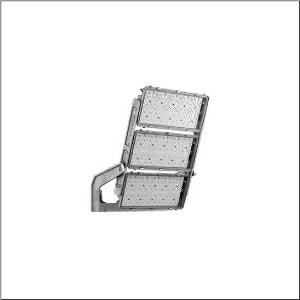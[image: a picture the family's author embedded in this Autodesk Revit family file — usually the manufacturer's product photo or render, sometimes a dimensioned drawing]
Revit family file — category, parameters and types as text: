
# Revit family: floodlight_fl_11_maxi_pro_remote___pl64_5xa779524e01aa_eec4
name_source: partatom
category: Lighting Fixtures
units: mm (PartAtom-declared; Revit-internal decimal feet)

## family parameters
Cut with Voids When Loaded = No
Host = Face
Light Source = No
Part Type = Normal
Room Calculation Point = No
Round Connector Dimension = Use Diameter
Shared = No

## types (1)
- --- (1 x LED, 128450 lm, 1334.7 W, 5700K)
    Apparent Load = 1335 VA
    CIE Flux Codes = 28 80 98 100 100
    Color Rendering = 90
    Color Temperature = 5700K
    Default Elevation = 1800 mm
    Description = Floodlight FL 11  maxi  pro Remote floodlight; light control with lens of PMMA; cover panel of toughened safety glass, transparent; light distribution: PL64, asymmetric direct distribution, LED; colour temperature: 5700K, rated luminous flux: 128.450lm, colour rendering: CRI > 90, light colour: 957; luminous efficacy: 96lm/W; brightness control: DMX+RDM; with terminal, 6-pole, max. 2.5mm², mains connection: 220..240V/380..400V AC, 50/60Hz, surge voltage resistance: line to ground: 10kV, ECG replaceable separately, no afterglow with DALI off / DMX off command, LED unit replaceable without ESD environment, dustproof LED module, dimming range 10..100%; 1335W floodlight with 3x LED unit of diecast aluminium, coated grey; length: 713mm / width: 651mm / height: 338mm; mounting bracket, of diecast aluminium, uncoated, natural, equipment: Power, protection rating (complete): IP66; insulation class (complete): insulation class I (protective earthing); certification: CE, ENEC, VDE; ball protection: ball impact resistance with accessories, impact resistance: IK07; only for outdoor installations, rated ambient temperature 10°C, permissible operating ambient temperature: -40..+30°C, permissible storage temperature: -40..+85°Cpackaging unit: 1 piece

Light Distribution: PL64
    Height = 320 mm
    Lamp = 1 x LED
    Lamp Light Flux = 128450 lm
    Lamp Power = 1334.7 W
    Lamp count = 1
    Length = 1002 mm
    Luminous efficacy = 96 lm/W
    Manufacturer = Siteco
    ModVariant = No
    Model = 5XA779524E01AA
    Mounting Place = Ceiling
    Mounting Type = Surface mounted
    Number of Poles = 1
    OnlyDefault = Yes
    Power Factor = 1
    Product Name = Floodlight FL 11 maxi pro Remote | PL64
    Product group = floodlight | ceiling mounted
    ProductGroupID = 302
    Protection Class = Protection class I
    Protection Degree = IP 66
    RLX_Detail_Level = 1
    RLX_Emergency_Light_Flux = 0 lm
    RLX_Emergency_Type = 0
    RLX_Emergency_Type_DB = No
    RlxData = <blob elided: 52433 chars, md5=c89f3b99>
    Socket = socket
    Standby Power = 0 W
    System Light Flux = 128450 lm
    System Power = 1335 W
    Type Comments = factory setting: luminous flux: 100 % | dim-lin: 255 | 920 mA
    Type Image = l_1349141.jpg
    URL = http://relux.com
    VarID = @adj_118829
    Voltage = 0 V
    Weight = 0.00 kg
    Width = 655 mm

## geometry (parser evidence)
native form markers: Blend x4, Sweep x15
no freeform markers — native parametric forms only
